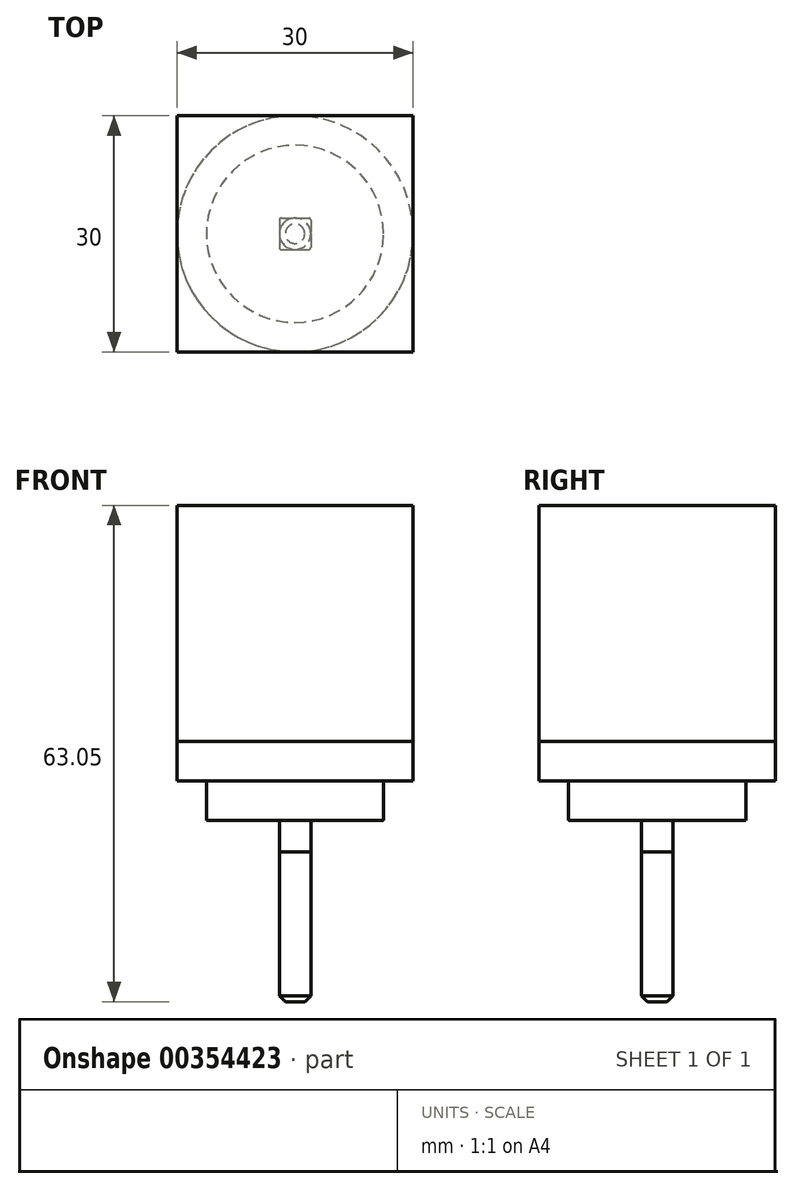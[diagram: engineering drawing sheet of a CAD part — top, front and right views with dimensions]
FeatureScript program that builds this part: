
annotation { "Feature Type Name" : "Feature", "Feature Type Description" : "" }
export const myFeature = defineFeature(function(context is Context, id is Id, definition is map)
    precondition{}
    {
        {
            var Q0;
            Q0=qCreatedBy(makeId("Top.planeOp"),FACE);
            var sketch = newSketch(context, id + "F0", { "sketchPlane" : qUnion([Q0])});
            skLineSegment(sketch, "E0.bottom", {"start": v(15, 15) * mm, "end": v(-15, 15) * mm});
            skLineSegment(sketch, "E0.top", {"start": v(15, -15) * mm, "end": v(-15, -15) * mm});
            skLineSegment(sketch, "E0.left", {"start": v(15, 15) * mm, "end": v(15, -15) * mm});
            skLineSegment(sketch, "E0.right", {"start": v(-15, 15) * mm, "end": v(-15, -15) * mm});
            skPoint(sketch, "E0.middle", {"position": v(0, 0) * mm});
            skSolve(sketch);
        }
        {
            var Q0;
            Q0=makeQuery(id+"F0.imprint","IMPRINT",FACE,{"disambiguationData":[TD([[makeQuery(id+"F0.imprint","IMPRINT",EDGE,{"derivedFrom":sQuery(id+"F0.wireOp",EDGE,"E0.bottom")}),1.0]])]});
            extrude(context, id + "F1", {"entities" : qUnion([Q0]), "depth" : 30 * mm});
        }
        {
            var Q0;
            Q0=makeQuery(id+"F1.opExtrude","CAP_FACE",FACE,{"disambiguationData":[OSD([sQuery(id+"F0.wireOp",EDGE,"E0.bottom"),sQuery(id+"F0.wireOp",EDGE,"E0.top"),sQuery(id+"F0.wireOp",EDGE,"E0.left"),sQuery(id+"F0.wireOp",EDGE,"E0.right")])],"isStart":true});
            var sketch = newSketch(context, id + "F2", { "sketchPlane" : qUnion([Q0])});
            skCircle(sketch, "E1", {"center": v(0, 0) * mm, "radius": 15 * mm});
            skSolve(sketch);
        }
        {
            var Q0;
            Q0 = qSketchRegion(id + "F2", true);
            extrude(context, id + "F3", {"entities" : qUnion([Q0]), "operationType" : NewBodyOperationType.ADD, "depth" : 5 * mm});
        }
        {
            var Q0;
            Q0=makeQuery(id+"F3.opExtrude","CAP_FACE",FACE,{"disambiguationData":[OSD([sQuery(id+"F2.wireOp",EDGE,"E1")])],"isStart":false});
            var sketch = newSketch(context, id + "F4", { "sketchPlane" : qUnion([Q0])});
            skCircle(sketch, "E2", {"center": v(0, 0) * mm, "radius": 11.25 * mm});
            skSolve(sketch);
        }
        {
            var Q0;
            Q0=makeQuery(id+"F4.imprint","IMPRINT",FACE,{"disambiguationData":[TD([[makeQuery(id+"F4.imprint","IMPRINT",EDGE,{"derivedFrom":sQuery(id+"F4.wireOp",EDGE,"E2")}),1.0]])]});
            extrude(context, id + "F5", {"entities" : qUnion([Q0]), "operationType" : NewBodyOperationType.ADD, "depth" : 5 * mm});
        }
        {
            var Q0;
            Q0=makeQuery(id+"F5.opExtrude","CAP_FACE",FACE,{"disambiguationData":[OSD([sQuery(id+"F4.wireOp",EDGE,"E2")])],"isStart":false});
            var sketch = newSketch(context, id + "F6", { "sketchPlane" : qUnion([Q0])});
            skLineSegment(sketch, "E3.bottom", {"start": v(-2, -2) * mm, "end": v(2, -2) * mm});
            skLineSegment(sketch, "E3.top", {"start": v(-2, 2) * mm, "end": v(2, 2) * mm});
            skLineSegment(sketch, "E3.left", {"start": v(-2, -2) * mm, "end": v(-2, 2) * mm});
            skLineSegment(sketch, "E3.right", {"start": v(2, -2) * mm, "end": v(2, 2) * mm});
            skPoint(sketch, "E3.middle", {"position": v(0, 0) * mm});
            skSolve(sketch);
        }
        {
            var Q0;
            Q0 = qSketchRegion(id + "F6", true);
            extrude(context, id + "F7", {"entities" : qUnion([Q0]), "operationType" : NewBodyOperationType.ADD, "depth" : 4 * mm});
        }
        {
            var Q0;
            Q0=makeQuery(id+"F7.opExtrude","CAP_FACE",FACE,{"disambiguationData":[OSD([sQuery(id+"F6.wireOp",EDGE,"E3.bottom"),sQuery(id+"F6.wireOp",EDGE,"E3.top"),sQuery(id+"F6.wireOp",EDGE,"E3.left"),sQuery(id+"F6.wireOp",EDGE,"E3.right")])],"isStart":false});
            var sketch = newSketch(context, id + "F8", { "sketchPlane" : qUnion([Q0])});
            skCircle(sketch, "E4", {"center": v(0, 0) * mm, "radius": 2 * mm});
            skSolve(sketch);
        }
        {
            var Q0;
            Q0 = qSketchRegion(id + "F8", true);
            extrude(context, id + "F9", {"entities" : qUnion([Q0]), "operationType" : NewBodyOperationType.ADD, "depth" : 19.05 * mm});
        }
        {
            var Q0;
            Q0=makeQuery(id+"F9.opExtrude","CAP_EDGE",EDGE,{"disambiguationData":[OSD([sQuery(id+"F8.wireOp",EDGE,"E4")])],"isStart":false});
            chamfer(context, id + "F10", {"entities" : qUnion([Q0]), "width" : 0.76 * mm, "tangentPropagation" : true});
        }
        {
            var Q0;
            Q0=makeQuery(id+"F7.opExtrude","SWEPT_EDGE",EDGE,{"disambiguationData":[OSD([sQuery(id+"F6.wireOp",EDGE,"E3.bottom"),sQuery(id+"F6.wireOp",EDGE,"E3.left")])]});
            var Q1;
            Q1=makeQuery(id+"F7.opExtrude","SWEPT_EDGE",EDGE,{"disambiguationData":[OSD([sQuery(id+"F6.wireOp",EDGE,"E3.top"),sQuery(id+"F6.wireOp",EDGE,"E3.left")])]});
            var Q2;
            Q2=makeQuery(id+"F7.opExtrude","SWEPT_EDGE",EDGE,{"disambiguationData":[OSD([sQuery(id+"F6.wireOp",EDGE,"E3.top"),sQuery(id+"F6.wireOp",EDGE,"E3.right")])]});
            var Q3;
            Q3=makeQuery(id+"F7.opExtrude","SWEPT_EDGE",EDGE,{"disambiguationData":[OSD([sQuery(id+"F6.wireOp",EDGE,"E3.bottom"),sQuery(id+"F6.wireOp",EDGE,"E3.right")])]});
            fillet(context, id + "F11", {"entities" : qUnion([Q0, Q1, Q2, Q3]), "radius" : 0.25 * mm, "tangentPropagation" : true, "allowEdgeOverflow" : false});
        }
    });
